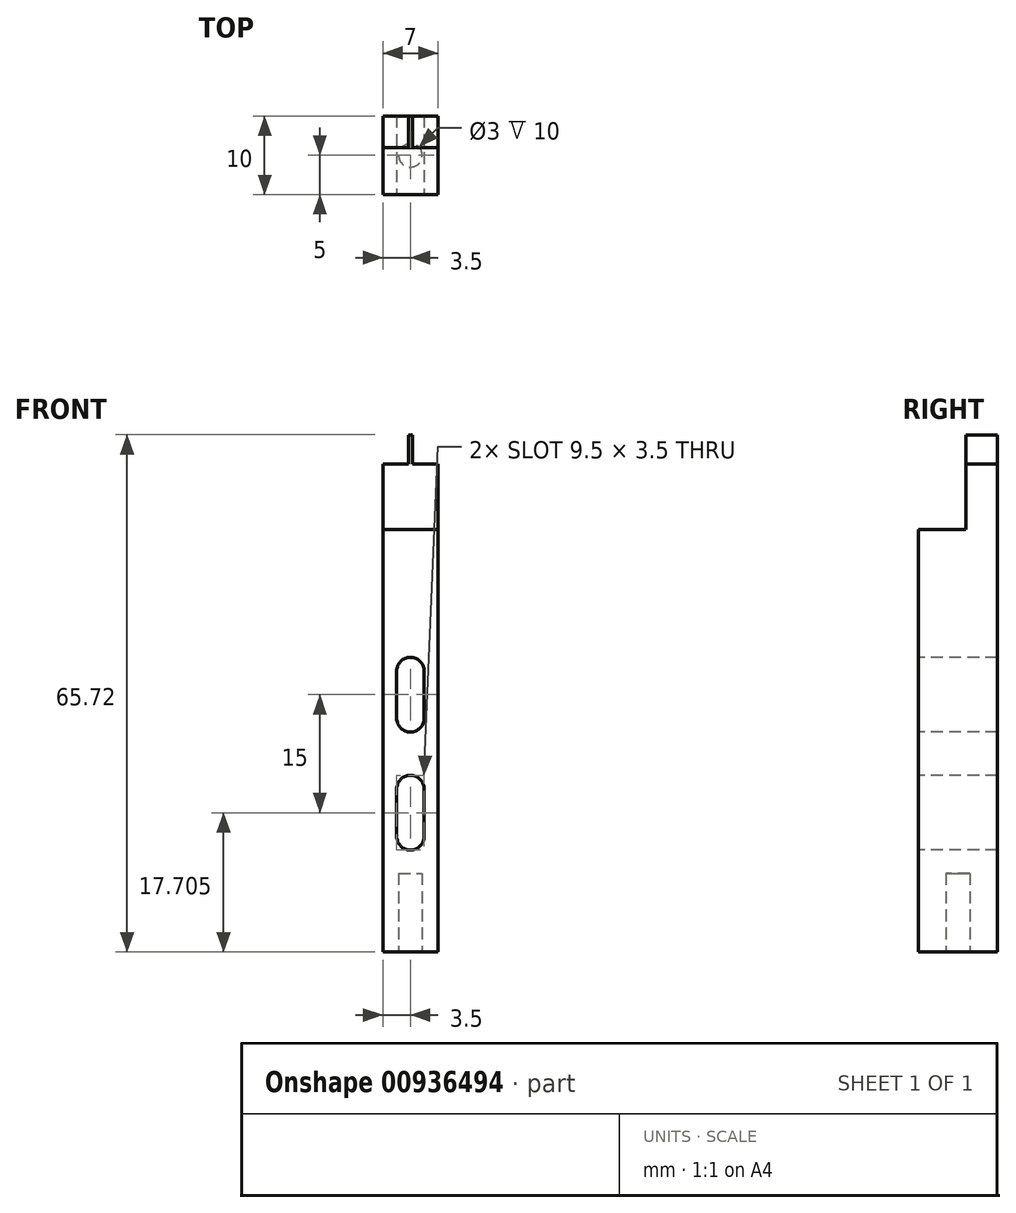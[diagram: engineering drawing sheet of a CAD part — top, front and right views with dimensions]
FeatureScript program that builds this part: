
annotation { "Feature Type Name" : "Feature", "Feature Type Description" : "" }
export const myFeature = defineFeature(function(context is Context, id is Id, definition is map)
    precondition{}
    {
        {
            var Q0;
            Q0=qCreatedBy(makeId("Front.planeOp"),FACE);
            var sketch = newSketch(context, id + "F0", { "sketchPlane" : qUnion([Q0])});
            skLineSegment(sketch, "E0.bottom", {"start": v(3.5, -32.85) * mm, "end": v(-3.5, -32.85) * mm});
            skLineSegment(sketch, "E0.top", {"start": v(3.5, 32.86) * mm, "end": v(-3.5, 32.86) * mm});
            skLineSegment(sketch, "E0.left", {"start": v(3.5, -32.85) * mm, "end": v(3.5, 32.86) * mm});
            skLineSegment(sketch, "E0.right", {"start": v(-3.5, -32.85) * mm, "end": v(-3.5, 32.86) * mm});
            skPoint(sketch, "E0.middle", {"position": v(0, 0) * mm});
            skSolve(sketch);
        }
        {
            var Q0;
            Q0 = qSketchRegion(id + "F0", true);
            extrude(context, id + "F1", {"entities" : qUnion([Q0]), "oppositeDirection" : true, "depth" : 10 * mm, "offsetDistance" : 25 * mm});
        }
        {
            var Q0;
            Q0=makeQuery(id+"F1.opExtrude","CAP_FACE",FACE,{"disambiguationData":[OSD([sQuery(id+"F0.wireOp",EDGE,"E0.bottom"),sQuery(id+"F0.wireOp",EDGE,"E0.top"),sQuery(id+"F0.wireOp",EDGE,"E0.left"),sQuery(id+"F0.wireOp",EDGE,"E0.right")])],"isStart":true});
            var sketch = newSketch(context, id + "F2", { "sketchPlane" : qUnion([Q0])});
            skLineSegment(sketch, "E1.bottom", {"start": v(-3.5, 32.86) * mm, "end": v(-0.25, 32.86) * mm});
            skLineSegment(sketch, "E1.top", {"start": v(-3.5, 29.14) * mm, "end": v(-0.25, 29.14) * mm});
            skLineSegment(sketch, "E1.left", {"start": v(-3.5, 32.86) * mm, "end": v(-3.5, 29.14) * mm});
            skLineSegment(sketch, "E1.right", {"start": v(-0.25, 32.86) * mm, "end": v(-0.25, 29.14) * mm});
            skLineSegment(sketch, "E2.bottom", {"start": v(3.5, 32.86) * mm, "end": v(0.25, 32.86) * mm});
            skLineSegment(sketch, "E2.top", {"start": v(3.5, 29.14) * mm, "end": v(0.25, 29.14) * mm});
            skLineSegment(sketch, "E2.left", {"start": v(3.5, 32.86) * mm, "end": v(3.5, 29.14) * mm});
            skLineSegment(sketch, "E2.right", {"start": v(0.25, 32.86) * mm, "end": v(0.25, 29.14) * mm});
            skSolve(sketch);
        }
        {
            var Q0;
            Q0 = qSketchRegion(id + "F2", true);
            extrude(context, id + "F3", {"entities" : qUnion([Q0]), "operationType" : NewBodyOperationType.REMOVE, "endBound" : BoundingType.UP_TO_NEXT, "oppositeDirection" : true, "depth" : 25 * mm, "offsetDistance" : 25 * mm});
        }
        {
            var Q0;
            Q0=makeQuery(id+"F1.opExtrude","CAP_FACE",FACE,{"disambiguationData":[OSD([sQuery(id+"F0.wireOp",EDGE,"E0.bottom"),sQuery(id+"F0.wireOp",EDGE,"E0.top"),sQuery(id+"F0.wireOp",EDGE,"E0.left"),sQuery(id+"F0.wireOp",EDGE,"E0.right")])],"isStart":true});
            var sketch = newSketch(context, id + "F4", { "sketchPlane" : qUnion([Q0])});
            skArc(sketch, "E3", {"start": v(-1.75, -18.15) * mm, "mid": v(0, -19.9) * mm, "end": v(1.75, -18.15) * mm});
            skArc(sketch, "E4", {"start": v(1.75, -12.15) * mm, "mid": v(0, -10.4) * mm, "end": v(-1.75, -12.15) * mm});
            skLineSegment(sketch, "E5", {"start": v(-1.75, -12.15) * mm, "end": v(-1.75, -18.15) * mm});
            skLineSegment(sketch, "E6", {"start": v(1.75, -12.15) * mm, "end": v(1.75, -18.15) * mm});
            skLineSegment(sketch, "E7", {"start": v(-3.5, -32.85) * mm, "end": v(-3.5, -3.15) * mm});
            skArc(sketch, "E8", {"start": v(-1.75, -3.15) * mm, "mid": v(0, -4.9) * mm, "end": v(1.75, -3.15) * mm});
            skArc(sketch, "E9", {"start": v(1.75, 2.85) * mm, "mid": v(0, 4.6) * mm, "end": v(-1.75, 2.85) * mm});
            skLineSegment(sketch, "E10", {"start": v(-1.75, 2.85) * mm, "end": v(-1.75, -3.15) * mm});
            skLineSegment(sketch, "E11", {"start": v(1.75, 2.85) * mm, "end": v(1.75, -3.15) * mm});
            skSolve(sketch);
        }
        {
            var Q0;
            Q0 = qSketchRegion(id + "F4", true);
            extrude(context, id + "F5", {"entities" : qUnion([Q0]), "operationType" : NewBodyOperationType.REMOVE, "endBound" : BoundingType.UP_TO_NEXT, "oppositeDirection" : true, "depth" : 25 * mm, "offsetDistance" : 25 * mm});
        }
        {
            var Q0;
            Q0=makeQuery(id+"F1.opExtrude","SWEPT_FACE",FACE,{"disambiguationData":[OSD([sQuery(id+"F0.wireOp",EDGE,"E0.left")])]});
            var sketch = newSketch(context, id + "F6", { "sketchPlane" : qUnion([Q0])});
            skLineSegment(sketch, "E12.bottom", {"start": v(0, 20.85) * mm, "end": v(6, 20.85) * mm});
            skLineSegment(sketch, "E12.top", {"start": v(0, 32.86) * mm, "end": v(6, 32.86) * mm});
            skLineSegment(sketch, "E12.left", {"start": v(0, 20.85) * mm, "end": v(0, 32.86) * mm});
            skLineSegment(sketch, "E12.right", {"start": v(6, 20.85) * mm, "end": v(6, 32.86) * mm});
            skSolve(sketch);
        }
        {
            var Q0;
            Q0 = qSketchRegion(id + "F6", true);
            extrude(context, id + "F7", {"entities" : qUnion([Q0]), "operationType" : NewBodyOperationType.REMOVE, "endBound" : BoundingType.UP_TO_NEXT, "oppositeDirection" : true, "depth" : 25 * mm, "offsetDistance" : 25 * mm});
        }
        {
            var Q0;
            Q0=makeQuery(id+"F1.opExtrude","SWEPT_FACE",FACE,{"disambiguationData":[OSD([sQuery(id+"F0.wireOp",EDGE,"E0.bottom")])]});
            var sketch = newSketch(context, id + "F8", { "sketchPlane" : qUnion([Q0])});
            skLineSegment(sketch, "E13", {"start": v(-3.5, 0) * mm, "end": v(0, 0) * mm});
            skLineSegment(sketch, "E14", {"start": v(0, 0) * mm, "end": v(0, -5) * mm});
            skCircle(sketch, "E15", {"center": v(0, -5) * mm, "radius": 1.5 * mm});
            skSolve(sketch);
        }
        {
            var Q0;
            Q0 = qSketchRegion(id + "F8", true);
            extrude(context, id + "F9", {"entities" : qUnion([Q0]), "operationType" : NewBodyOperationType.REMOVE, "oppositeDirection" : true, "depth" : 10 * mm, "offsetDistance" : 25 * mm});
        }
    });
